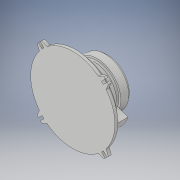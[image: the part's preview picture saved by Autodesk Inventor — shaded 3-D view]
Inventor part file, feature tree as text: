
AUTODESK INVENTOR PART (.ipt)
format: ipt  version: 2017 (Build 210142000, 142)  size: 267,264 bytes
history: native  units: in
note: dims shown in document units (in); Inventor stores cm internally (conversion verified against a paired STEP export)
features: extrude x8, sketch x8, projected_geometry x3, other x2, plane x1, loft x1
ambient origin geometry x8: Origin, YZ Plane, XZ Plane, XY Plane, X Axis, Y Axis, Z Axis, Center Point
bodies: Solid1 (feature_tree)
feature tree (23):
  extrude  "Extrusion1"  Depth=0.5906in TaperAngle=0.0deg
  extrude  "Extrusion2"  Depth=0.1772in TaperAngle=0.0deg
  extrude  "Extrusion3"  [1 undecoded]
  plane  "Work Plane1"
  extrude  "Extrusion4"  Depth=0.3346in TaperAngle=0.0deg
  loft  "Loft1"
  extrude  "Extrusion5"  Depth=0.1374in
  extrude  "Extrusion6"  Depth=0.8071in TaperAngle=0.0deg
  extrude  "Extrusion7"  Depth=0.2165in TaperAngle=0.0deg
  extrude  "Extrusion8"  TaperAngle=45.0deg  [1 undecoded]
  sketch  "Sketch1"  dims[d0=3.5433in d1=0.5906in d2=0.0in]
  sketch  "Sketch2"  dims[d3=3.2677in d4=0.1772in d5=0.0in]
  sketch  "Sketch3"  dims[d6=0.1772in d7=0.0in d8=-2.3425in]
  sketch  "Sketch4"  dims[d9=5.4724in d10=0.3346in d11=0.0in]
  other  "Edges1"
  other  "Edges2"
  sketch  "Sketch5"  dims[d12=0.0in d13=90.0deg d14=0.0in d15=90.0deg]
  projected_geometry  "Projected Loop1"
  projected_geometry  "Projected Loop2"
  sketch  "Sketch6"  dims[d16=0.8268in d17=0.1374in]
  sketch  "Sketch7"  dims[d18=0.3436in d19=0.8071in d20=0.0in]
  projected_geometry  "Projected Loop3"
  sketch  "Sketch9"  dims[d21=6.25in d22=0.2165in d23=0.0in d24=45.0deg d25=45.0deg d26=0.1969in d27=0.1969in d28=0.4331in d29=0.4331in d30=4.3425in d31=0.1969in d32=0.1969in d33=0.4331in d34=0.4331in d35=4.3425in d36=0.1378in d37=0.3071in d38=0.1378in d39=0.3071in d40=0.1378in d41=0.1378in d42=0.3071in d43=0.3071in d44=0.1378in d45=0.1378in d46=0.3071in d47=0.3071in d48=0.1378in d49=0.1378in d50=0.3071in d51=0.3071in d52=0.2165in d53=0.0in d54=0.25in d55=0.25in d56=0.25in d57=0.0in]
note: 2 required parameter values undecoded (feature->parameter linkage not recoverable at this tier; creation-order binding heuristic only, values carry confidence <= 0.55)
